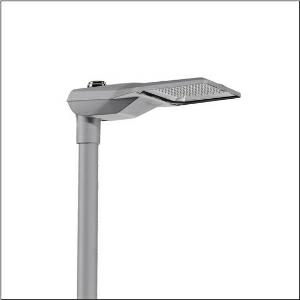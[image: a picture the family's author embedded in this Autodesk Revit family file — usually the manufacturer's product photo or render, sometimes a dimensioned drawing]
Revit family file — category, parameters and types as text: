
# Revit family: streetlight_sl_21_midi___st1_5a_5xe7p37n08lb_8b0d
name_source: partatom
category: Lighting Fixtures
units: mm (PartAtom-declared; Revit-internal decimal feet)

## family parameters
Cut with Voids When Loaded = No
Host = Face
Light Source = No
Part Type = Normal
Room Calculation Point = No
Round Connector Dimension = Use Diameter
Shared = No

## types (1)
- --- (1 x LED, 14100 lm, 98.3 W, 3000K)
    Apparent Load = 98 VA
    CIE Flux Codes = 22 53 95 100 100
    Color Rendering = 70
    Color Temperature = 3000K
    Default Elevation = 1800 mm
    Description = Streetlight SL 21 midi, mast luminaire, primary light control with lens, of PMMA, primary optical cover: cover, of toughened safety glass, transparent, light distribution: ST1.5a, light emission: direct distribution, primary light characteristic: asymmetric, installation type: side-entry, LED, 3G 2.5mm², High Power LED, rated luminous flux: 14.100lm, luminous efficacy: 143lm/W, light colour: 730, colour temperature: 3000K, control gear: NEMA (7pin), control: overheat protection, pre-setting: linear dimming characteristic, constant luminous flux control, time-dependent luminous flux control, flexible luminous flux parameterisation, mains connection: 220..240V, AC, 50/60Hz, connection cable pre-assembled, cable length: 10,5m, wiring characteristics: H05VV-F, start of lifetime: 98W, end of service life: 101W, reduction: 45W, luminaire housing, of diecast aluminium (EN AC-44300), powder-coated, Siteco® metallic grey (DB 702S), corrosivity category C5 mid according to DIN EN ISO 12944, multi-level sealing system, sealing non-destructively replaceable, inclination adjustable: 0°, 5°, 10°, 15°, length: 644mm, width: 335mm, height: 110mm, spigot size: 42mm (side-entry), mounting height: 4..8m, protection rating (complete): IP66, insulation class (complete): insulation class I (protective earthing), certification: CE, ENEC, ENEC+, VDE, impact resistance: IK10, permissible operating ambient temperature for outdoor applications: -40..+50°C, standard-compliant lighting for roads and squares, packaging unit: 1 piece

Light Distribution: ST1.5a
    Height = 111 mm
    Lamp = 1 x LED
    Lamp Light Flux = 14100 lm
    Lamp Power = 98.3 W
    Lamp count = 1
    Length = 644 mm
    Luminous efficacy = 143 lm/W
    Manufacturer = Siteco
    ModVariant = No
    Model = 5XE7P37N08LB
    Number of Poles = 1
    OnlyDefault = Yes
    Power Factor = 1
    Product Name = Streetlight SL 21 midi | ST1.5a
    Product group = mast luminaire | pylon top
    ProductGroupID = 6100
    Protection Class = Protection class I
    Protection Degree = IP 66
    RLX_Detail_Level = 1
    RLX_Emergency_Light_Flux = 0 lm
    RLX_Emergency_Type = 0
    RLX_Emergency_Type_DB = No
    RlxData = <blob elided: 30209 chars, md5=92ba5889>
    Socket = socket
    Standby Power = 0 W
    System Light Flux = 14100 lm
    System Power = 98 W
    Type Comments = factory setting: luminous flux: 100 % | dim-lin: 254 | 1020 mA
    Type Image = l_1294377.jpg
    URL = http://relux.com
    VarID = @adj_133500
    Voltage = 0 V
    Weight = 0.00 kg
    Width = 336 mm

## geometry (parser evidence)
native form markers: Blend x4, Sweep x8
no freeform markers — native parametric forms only
